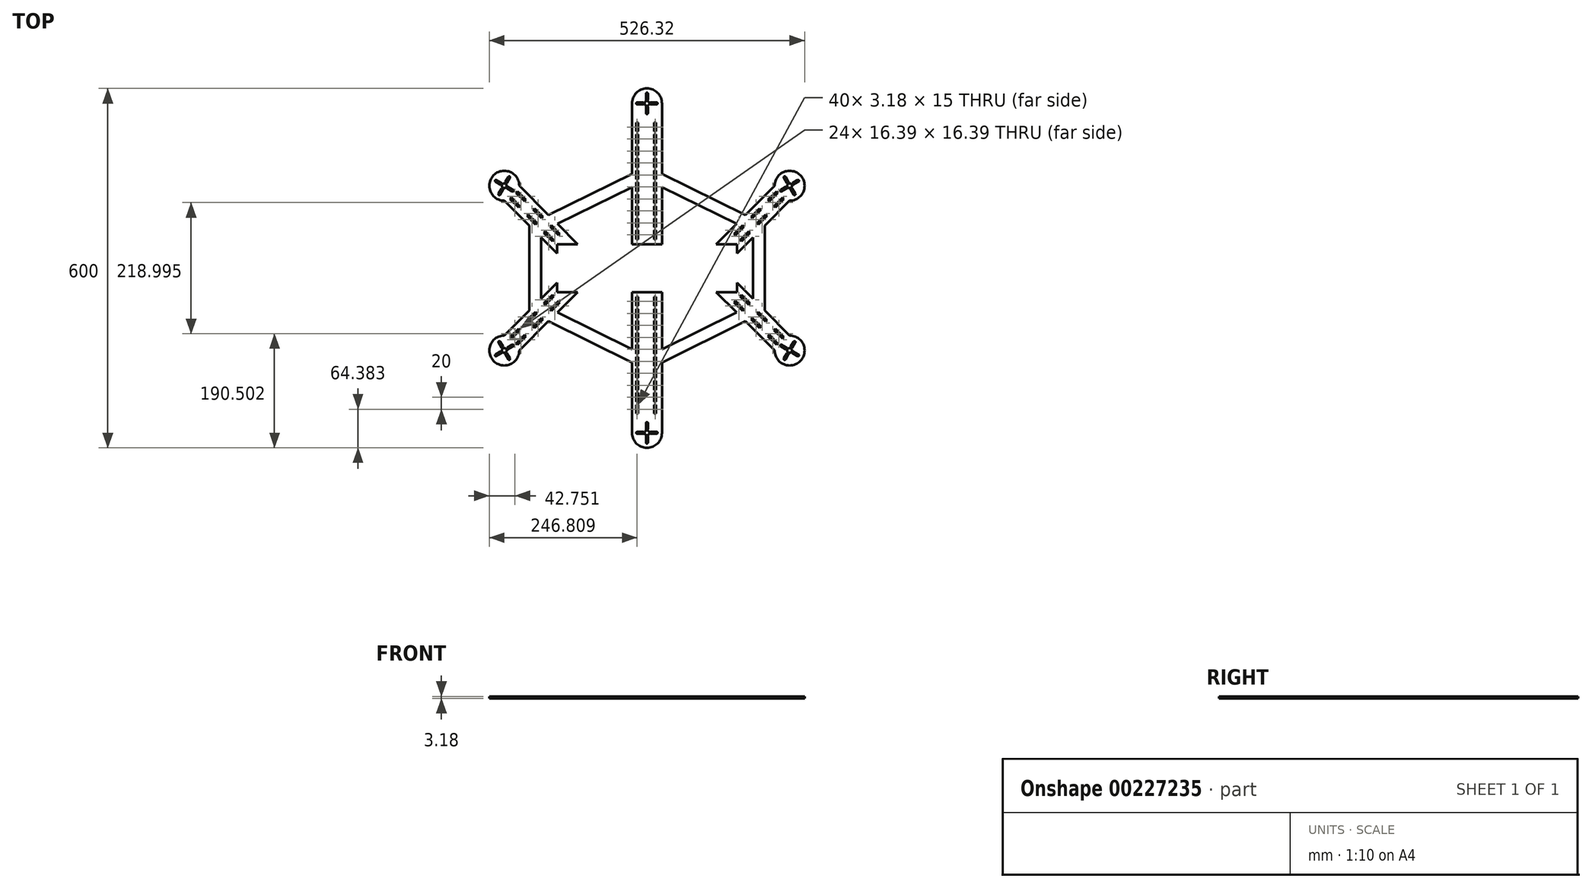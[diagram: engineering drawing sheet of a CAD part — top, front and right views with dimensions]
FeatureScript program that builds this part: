
annotation { "Feature Type Name" : "Feature", "Feature Type Description" : "" }
export const myFeature = defineFeature(function(context is Context, id is Id, definition is map)
    precondition{}
    {
        {
            var Q0;
            Q0=qCreatedBy(makeId("Top.planeOp"),FACE);
            var sketch = newSketch(context, id + "F0", { "sketchPlane" : qUnion([Q0])});
            skPoint(sketch, "E0.middle", {"position": v(0, 0) * mm});
            skCircle(sketch, "E1", {"center": v(0, 275) * mm, "radius": 25 * mm});
            skPoint(sketch, "E1.centerSnap0", {"position": v(0, 301.8) * mm});
            skCircle(sketch, "E2.1.0", {"center": v(-238.16, 137.5) * mm, "radius": 25 * mm});
            skLineSegment(sketch, "E3.bottom", {"start": v(150, -40) * mm, "end": v(-150, -40) * mm});
            skLineSegment(sketch, "E3.top", {"start": v(150, 40) * mm, "end": v(-150, 40) * mm});
            skLineSegment(sketch, "E3.left", {"start": v(150, -40) * mm, "end": v(150, 40) * mm});
            skLineSegment(sketch, "E3.right", {"start": v(-150, -40) * mm, "end": v(-150, 40) * mm});
            skLineSegment(sketch, "E4", {"start": v(-213.16, 137.5) * mm, "end": v(-115.66, 40) * mm});
            skLineSegment(sketch, "E5", {"start": v(-263.16, 137.5) * mm, "end": v(-150, 24.34) * mm});
            skCircle(sketch, "E6.MirrorC", {"center": v(-238.16, -137.5) * mm, "radius": 25 * mm});
            skLineSegment(sketch, "E7", {"start": v(0, 0) * mm, "end": v(0, 86.77) * mm, "construction": true});
            skLineSegment(sketch, "E8.MirrorCS", {"start": v(213.16, 137.5) * mm, "end": v(115.66, 40) * mm});
            skLineSegment(sketch, "E9.MirrorCS", {"start": v(263.16, 137.5) * mm, "end": v(150, 24.34) * mm});
            skCircle(sketch, "E10.MirrorC", {"center": v(238.16, 137.5) * mm, "radius": 25 * mm});
            skCircle(sketch, "E11.MirrorC", {"center": v(238.16, -137.5) * mm, "radius": 25 * mm});
            skLineSegment(sketch, "E12", {"start": v(0, 0) * mm, "end": v(-288.43, 0) * mm, "construction": true});
            skCircle(sketch, "E13.MirrorC", {"center": v(0, -275) * mm, "radius": 25 * mm});
            skLineSegment(sketch, "E14.bottom", {"start": v(-25, 275) * mm, "end": v(25, 275) * mm});
            skLineSegment(sketch, "E14.top", {"start": v(-25, 40) * mm, "end": v(25, 40) * mm});
            skLineSegment(sketch, "E14.left", {"start": v(-25, 275) * mm, "end": v(-25, 40) * mm});
            skLineSegment(sketch, "E14.right", {"start": v(25, 275) * mm, "end": v(25, 40) * mm});
            skLineSegment(sketch, "E15.MirrorCS", {"start": v(-25, -275) * mm, "end": v(-25, -40) * mm});
            skLineSegment(sketch, "E16.MirrorCS", {"start": v(25, -275) * mm, "end": v(25, -40) * mm});
            skLineSegment(sketch, "E17", {"start": v(-25, 157.5) * mm, "end": v(-25, 135.2) * mm});
            skLineSegment(sketch, "E18.MirrorCS", {"start": v(-213.16, -137.5) * mm, "end": v(-115.66, -40) * mm});
            skLineSegment(sketch, "E19.MirrorCS", {"start": v(-263.16, -137.5) * mm, "end": v(-150, -24.34) * mm});
            skLineSegment(sketch, "E20.MirrorCS", {"start": v(263.16, -137.5) * mm, "end": v(150, -24.34) * mm});
            skLineSegment(sketch, "E21.MirrorCS", {"start": v(213.16, -137.5) * mm, "end": v(115.66, -40) * mm});
            skLineSegment(sketch, "E22", {"start": v(-164.4, 88.75) * mm, "end": v(-25, 157.5) * mm});
            skLineSegment(sketch, "E23", {"start": v(-25, 135.2) * mm, "end": v(-149.47, 73.82) * mm});
            skLineSegment(sketch, "E24.MirrorCS", {"start": v(25, 135.2) * mm, "end": v(149.47, 73.82) * mm});
            skLineSegment(sketch, "E25.MirrorCS", {"start": v(164.4, 88.75) * mm, "end": v(25, 157.5) * mm});
            skLineSegment(sketch, "E26.MirrorCS", {"start": v(-25, -135.2) * mm, "end": v(-149.47, -73.82) * mm});
            skLineSegment(sketch, "E27.MirrorCS", {"start": v(-164.4, -88.75) * mm, "end": v(-25, -157.5) * mm});
            skLineSegment(sketch, "E28.MirrorCS", {"start": v(164.4, -88.75) * mm, "end": v(25, -157.5) * mm});
            skLineSegment(sketch, "E29.MirrorCS", {"start": v(25, -135.2) * mm, "end": v(149.47, -73.82) * mm});
            skLineSegment(sketch, "E30", {"start": v(-164.6, -38.94) * mm, "end": v(-188.74, -63.09) * mm});
            skLineSegment(sketch, "E31", {"start": v(-188.74, 63.09) * mm, "end": v(-164.6, 38.94) * mm});
            skLineSegment(sketch, "E32.MirrorCS", {"start": v(188.74, 63.09) * mm, "end": v(164.6, 38.94) * mm});
            skLineSegment(sketch, "E33", {"start": v(-176.67, 51.01) * mm, "end": v(-176.67, -51.01) * mm});
            skLineSegment(sketch, "E34", {"start": v(-196.67, 71.01) * mm, "end": v(-196.67, -71.01) * mm});
            skLineSegment(sketch, "E35.MirrorCS", {"start": v(176.67, 51.01) * mm, "end": v(176.67, -51.01) * mm});
            skLineSegment(sketch, "E36.MirrorCS", {"start": v(196.67, 71.01) * mm, "end": v(196.67, -71.01) * mm});
            skSolve(sketch);
        }
        {
            var Q0;
            Q0 = qSketchRegion(id + "F0", true);
            var Q1;
            {var subQ2=sQuery(id+"F0.wireOp",EDGE,"E14.top");Q1=makeQuery(id+"F0.imprint","IMPRINT",FACE,{"disambiguationData":[TD([[makeQuery(id+"F0.imprint","IMPRINT",EDGE,{"derivedFrom":subQ2}),-1.0]])]});}
            extrude(context, id + "F1", {"entities" : qUnion([Q0, Q1]), "depth" : 3.17 * mm});
        }
        {
            var Q0;
            Q0=makeQuery(id+"F1.opExtrude","CAP_FACE",FACE,{"disambiguationData":[OSD([sQuery(id+"F0.wireOp",EDGE,"E1"),sQuery(id+"F0.wireOp",EDGE,"E2.1.0"),sQuery(id+"F0.wireOp",EDGE,"E3.bottom"),sQuery(id+"F0.wireOp",EDGE,"E3.top"),sQuery(id+"F0.wireOp",EDGE,"E3.left"),sQuery(id+"F0.wireOp",EDGE,"E3.right"),sQuery(id+"F0.wireOp",EDGE,"E4"),sQuery(id+"F0.wireOp",EDGE,"E5"),sQuery(id+"F0.wireOp",EDGE,"E6.MirrorC"),sQuery(id+"F0.wireOp",EDGE,"E8.MirrorCS"),sQuery(id+"F0.wireOp",EDGE,"E9.MirrorCS"),sQuery(id+"F0.wireOp",EDGE,"E10.MirrorC"),sQuery(id+"F0.wireOp",EDGE,"E11.MirrorC"),sQuery(id+"F0.wireOp",EDGE,"E13.MirrorC"),sQuery(id+"F0.wireOp",EDGE,"E14.left"),sQuery(id+"F0.wireOp",EDGE,"E14.right"),sQuery(id+"F0.wireOp",EDGE,"E15.MirrorCS"),sQuery(id+"F0.wireOp",EDGE,"E16.MirrorCS"),sQuery(id+"F0.wireOp",EDGE,"E18.MirrorCS"),sQuery(id+"F0.wireOp",EDGE,"E19.MirrorCS"),sQuery(id+"F0.wireOp",EDGE,"E21.MirrorCS"),sQuery(id+"F0.wireOp",EDGE,"E22"),sQuery(id+"F0.wireOp",EDGE,"E23"),sQuery(id+"F0.wireOp",EDGE,"E24.MirrorCS"),sQuery(id+"F0.wireOp",EDGE,"E25.MirrorCS"),sQuery(id+"F0.wireOp",EDGE,"E26.MirrorCS"),sQuery(id+"F0.wireOp",EDGE,"E27.MirrorCS"),sQuery(id+"F0.wireOp",EDGE,"E28.MirrorCS"),sQuery(id+"F0.wireOp",EDGE,"E29.MirrorCS"),sQuery(id+"F0.wireOp",EDGE,"E30"),sQuery(id+"F0.wireOp",EDGE,"E31"),sQuery(id+"F0.wireOp",EDGE,"E32.MirrorCS"),sQuery(id+"F0.wireOp",EDGE,"E20.MirrorCS"),sQuery(id+"F0.wireOp",EDGE,"E33"),sQuery(id+"F0.wireOp",EDGE,"E34"),sQuery(id+"F0.wireOp",EDGE,"E35.MirrorCS"),sQuery(id+"F0.wireOp",EDGE,"E36.MirrorCS")])],"isStart":false});
            var sketch = newSketch(context, id + "F2", { "sketchPlane" : qUnion([Q0])});
            skLineSegment(sketch, "E37.bottom", {"start": v(-17.94, 243.12) * mm, "end": v(-14.76, 243.12) * mm});
            skLineSegment(sketch, "E37.top", {"start": v(-17.94, 228.12) * mm, "end": v(-14.76, 228.12) * mm});
            skLineSegment(sketch, "E37.left", {"start": v(-17.94, 243.12) * mm, "end": v(-17.94, 228.12) * mm});
            skLineSegment(sketch, "E37.right", {"start": v(-14.76, 243.12) * mm, "end": v(-14.76, 228.12) * mm});
            skLineSegment(sketch, "E38.1.0.0", {"start": v(12.06, 243.12) * mm, "end": v(15.24, 243.12) * mm});
            skLineSegment(sketch, "E38.1.0.1", {"start": v(12.06, 243.12) * mm, "end": v(12.06, 228.12) * mm});
            skLineSegment(sketch, "E38.1.0.2", {"start": v(15.24, 243.12) * mm, "end": v(15.24, 228.12) * mm});
            skLineSegment(sketch, "E38.1.0.3", {"start": v(12.06, 228.12) * mm, "end": v(15.24, 228.12) * mm});
            skLineSegment(sketch, "E38.direction1", {"start": v(-17.94, 243.12) * mm, "end": v(12.06, 243.12) * mm, "construction": true});
            skLineSegment(sketch, "E39.0.1.0", {"start": v(-17.94, 223.12) * mm, "end": v(12.06, 223.12) * mm, "construction": true});
            skLineSegment(sketch, "E39.0.1.1", {"start": v(-14.76, 223.12) * mm, "end": v(-14.76, 208.12) * mm});
            skLineSegment(sketch, "E39.0.1.2", {"start": v(-17.94, 223.12) * mm, "end": v(-17.94, 208.12) * mm});
            skLineSegment(sketch, "E39.0.1.3", {"start": v(15.24, 223.12) * mm, "end": v(15.24, 208.12) * mm});
            skLineSegment(sketch, "E39.0.1.4", {"start": v(12.06, 223.12) * mm, "end": v(12.06, 208.12) * mm});
            skLineSegment(sketch, "E39.0.1.5", {"start": v(12.06, 208.12) * mm, "end": v(15.24, 208.12) * mm});
            skLineSegment(sketch, "E39.0.1.6", {"start": v(-17.94, 223.12) * mm, "end": v(-14.76, 223.12) * mm});
            skLineSegment(sketch, "E39.0.1.7", {"start": v(-17.94, 208.12) * mm, "end": v(-14.76, 208.12) * mm});
            skLineSegment(sketch, "E39.0.1.8", {"start": v(12.06, 223.12) * mm, "end": v(15.24, 223.12) * mm});
            skLineSegment(sketch, "E39.0.2.0", {"start": v(-17.94, 203.12) * mm, "end": v(12.06, 203.12) * mm, "construction": true});
            skLineSegment(sketch, "E39.0.2.1", {"start": v(-14.76, 203.12) * mm, "end": v(-14.76, 188.12) * mm});
            skLineSegment(sketch, "E39.0.2.2", {"start": v(-17.94, 203.12) * mm, "end": v(-17.94, 188.12) * mm});
            skLineSegment(sketch, "E39.0.2.3", {"start": v(15.24, 203.12) * mm, "end": v(15.24, 188.12) * mm});
            skLineSegment(sketch, "E39.0.2.4", {"start": v(12.06, 203.12) * mm, "end": v(12.06, 188.12) * mm});
            skLineSegment(sketch, "E39.0.2.5", {"start": v(12.06, 188.12) * mm, "end": v(15.24, 188.12) * mm});
            skLineSegment(sketch, "E39.0.2.6", {"start": v(-17.94, 203.12) * mm, "end": v(-14.76, 203.12) * mm});
            skLineSegment(sketch, "E39.0.2.7", {"start": v(-17.94, 188.12) * mm, "end": v(-14.76, 188.12) * mm});
            skLineSegment(sketch, "E39.0.2.8", {"start": v(12.06, 203.12) * mm, "end": v(15.24, 203.12) * mm});
            skLineSegment(sketch, "E39.0.3.0", {"start": v(-17.94, 183.12) * mm, "end": v(12.06, 183.12) * mm, "construction": true});
            skLineSegment(sketch, "E39.0.3.1", {"start": v(-14.76, 183.12) * mm, "end": v(-14.76, 168.12) * mm});
            skLineSegment(sketch, "E39.0.3.2", {"start": v(-17.94, 183.12) * mm, "end": v(-17.94, 168.12) * mm});
            skLineSegment(sketch, "E39.0.3.3", {"start": v(15.24, 183.12) * mm, "end": v(15.24, 168.12) * mm});
            skLineSegment(sketch, "E39.0.3.4", {"start": v(12.06, 183.12) * mm, "end": v(12.06, 168.12) * mm});
            skLineSegment(sketch, "E39.0.3.5", {"start": v(12.06, 168.12) * mm, "end": v(15.24, 168.12) * mm});
            skLineSegment(sketch, "E39.0.3.6", {"start": v(-17.94, 183.12) * mm, "end": v(-14.76, 183.12) * mm});
            skLineSegment(sketch, "E39.0.3.7", {"start": v(-17.94, 168.12) * mm, "end": v(-14.76, 168.12) * mm});
            skLineSegment(sketch, "E39.0.3.8", {"start": v(12.06, 183.12) * mm, "end": v(15.24, 183.12) * mm});
            skLineSegment(sketch, "E39.0.4.0", {"start": v(-17.94, 163.12) * mm, "end": v(12.06, 163.12) * mm, "construction": true});
            skLineSegment(sketch, "E39.0.4.1", {"start": v(-14.76, 163.12) * mm, "end": v(-14.76, 148.12) * mm});
            skLineSegment(sketch, "E39.0.4.2", {"start": v(-17.94, 163.12) * mm, "end": v(-17.94, 148.12) * mm});
            skLineSegment(sketch, "E39.0.4.3", {"start": v(15.24, 163.12) * mm, "end": v(15.24, 148.12) * mm});
            skLineSegment(sketch, "E39.0.4.4", {"start": v(12.06, 163.12) * mm, "end": v(12.06, 148.12) * mm});
            skLineSegment(sketch, "E39.0.4.5", {"start": v(12.06, 148.12) * mm, "end": v(15.24, 148.12) * mm});
            skLineSegment(sketch, "E39.0.4.6", {"start": v(-17.94, 163.12) * mm, "end": v(-14.76, 163.12) * mm});
            skLineSegment(sketch, "E39.0.4.7", {"start": v(-17.94, 148.12) * mm, "end": v(-14.76, 148.12) * mm});
            skLineSegment(sketch, "E39.0.4.8", {"start": v(12.06, 163.12) * mm, "end": v(15.24, 163.12) * mm});
            skLineSegment(sketch, "E39.0.5.0", {"start": v(-17.94, 143.12) * mm, "end": v(12.06, 143.12) * mm, "construction": true});
            skLineSegment(sketch, "E39.0.5.1", {"start": v(-14.76, 143.12) * mm, "end": v(-14.76, 128.12) * mm});
            skLineSegment(sketch, "E39.0.5.2", {"start": v(-17.94, 143.12) * mm, "end": v(-17.94, 128.12) * mm});
            skLineSegment(sketch, "E39.0.5.3", {"start": v(15.24, 143.12) * mm, "end": v(15.24, 128.12) * mm});
            skLineSegment(sketch, "E39.0.5.4", {"start": v(12.06, 143.12) * mm, "end": v(12.06, 128.12) * mm});
            skLineSegment(sketch, "E39.0.5.5", {"start": v(12.06, 128.12) * mm, "end": v(15.24, 128.12) * mm});
            skLineSegment(sketch, "E39.0.5.6", {"start": v(-17.94, 143.12) * mm, "end": v(-14.76, 143.12) * mm});
            skLineSegment(sketch, "E39.0.5.7", {"start": v(-17.94, 128.12) * mm, "end": v(-14.76, 128.12) * mm});
            skLineSegment(sketch, "E39.0.5.8", {"start": v(12.06, 143.12) * mm, "end": v(15.24, 143.12) * mm});
            skLineSegment(sketch, "E39.0.6.0", {"start": v(-17.94, 123.12) * mm, "end": v(12.06, 123.12) * mm, "construction": true});
            skLineSegment(sketch, "E39.0.6.1", {"start": v(-14.76, 123.12) * mm, "end": v(-14.76, 108.12) * mm});
            skLineSegment(sketch, "E39.0.6.2", {"start": v(-17.94, 123.12) * mm, "end": v(-17.94, 108.12) * mm});
            skLineSegment(sketch, "E39.0.6.3", {"start": v(15.24, 123.12) * mm, "end": v(15.24, 108.12) * mm});
            skLineSegment(sketch, "E39.0.6.4", {"start": v(12.06, 123.12) * mm, "end": v(12.06, 108.12) * mm});
            skLineSegment(sketch, "E39.0.6.5", {"start": v(12.06, 108.12) * mm, "end": v(15.24, 108.12) * mm});
            skLineSegment(sketch, "E39.0.6.6", {"start": v(-17.94, 123.12) * mm, "end": v(-14.76, 123.12) * mm});
            skLineSegment(sketch, "E39.0.6.7", {"start": v(-17.94, 108.12) * mm, "end": v(-14.76, 108.12) * mm});
            skLineSegment(sketch, "E39.0.6.8", {"start": v(12.06, 123.12) * mm, "end": v(15.24, 123.12) * mm});
            skLineSegment(sketch, "E39.0.7.0", {"start": v(-17.94, 103.12) * mm, "end": v(12.06, 103.12) * mm, "construction": true});
            skLineSegment(sketch, "E39.0.7.1", {"start": v(-14.76, 103.12) * mm, "end": v(-14.76, 88.12) * mm});
            skLineSegment(sketch, "E39.0.7.2", {"start": v(-17.94, 103.12) * mm, "end": v(-17.94, 88.12) * mm});
            skLineSegment(sketch, "E39.0.7.3", {"start": v(15.24, 103.12) * mm, "end": v(15.24, 88.12) * mm});
            skLineSegment(sketch, "E39.0.7.4", {"start": v(12.06, 103.12) * mm, "end": v(12.06, 88.12) * mm});
            skLineSegment(sketch, "E39.0.7.5", {"start": v(12.06, 88.12) * mm, "end": v(15.24, 88.12) * mm});
            skLineSegment(sketch, "E39.0.7.6", {"start": v(-17.94, 103.12) * mm, "end": v(-14.76, 103.12) * mm});
            skLineSegment(sketch, "E39.0.7.7", {"start": v(-17.94, 88.12) * mm, "end": v(-14.76, 88.12) * mm});
            skLineSegment(sketch, "E39.0.7.8", {"start": v(12.06, 103.12) * mm, "end": v(15.24, 103.12) * mm});
            skLineSegment(sketch, "E39.direction1", {"start": v(-17.94, 228.12) * mm, "end": v(7.06, 228.12) * mm, "construction": true});
            skLineSegment(sketch, "E39.direction2", {"start": v(-17.94, 228.12) * mm, "end": v(-17.94, 208.12) * mm, "construction": true});
            skLineSegment(sketch, "E40.MirrorCS", {"start": v(-17.94, -228.12) * mm, "end": v(-14.76, -228.12) * mm});
            skLineSegment(sketch, "E41.MirrorCS", {"start": v(-17.94, -223.12) * mm, "end": v(-14.76, -223.12) * mm});
            skLineSegment(sketch, "E42.MirrorCS", {"start": v(12.06, -223.12) * mm, "end": v(15.24, -223.12) * mm});
            skLineSegment(sketch, "E43.MirrorCS", {"start": v(-17.94, -208.12) * mm, "end": v(-14.76, -208.12) * mm});
            skLineSegment(sketch, "E44.MirrorCS", {"start": v(-17.94, -223.12) * mm, "end": v(-17.94, -208.12) * mm});
            skLineSegment(sketch, "E45.MirrorCS", {"start": v(12.06, -108.12) * mm, "end": v(15.24, -108.12) * mm});
            skLineSegment(sketch, "E46.MirrorCS", {"start": v(-17.94, -108.12) * mm, "end": v(-14.76, -108.12) * mm});
            skLineSegment(sketch, "E47.MirrorCS", {"start": v(12.06, -123.12) * mm, "end": v(15.24, -123.12) * mm});
            skLineSegment(sketch, "E48.MirrorCS", {"start": v(12.06, -228.12) * mm, "end": v(15.24, -228.12) * mm});
            skLineSegment(sketch, "E49.MirrorCS", {"start": v(-17.94, -183.12) * mm, "end": v(-14.76, -183.12) * mm});
            skLineSegment(sketch, "E50.MirrorCS", {"start": v(12.06, -103.12) * mm, "end": v(15.24, -103.12) * mm});
            skLineSegment(sketch, "E51.MirrorCS", {"start": v(-17.94, -148.12) * mm, "end": v(-14.76, -148.12) * mm});
            skLineSegment(sketch, "E52.MirrorCS", {"start": v(-17.94, -143.12) * mm, "end": v(-14.76, -143.12) * mm});
            skLineSegment(sketch, "E53.MirrorCS", {"start": v(-17.94, -103.12) * mm, "end": v(-14.76, -103.12) * mm});
            skLineSegment(sketch, "E54.MirrorCS", {"start": v(12.06, -183.12) * mm, "end": v(15.24, -183.12) * mm});
            skLineSegment(sketch, "E55.MirrorCS", {"start": v(12.06, -203.12) * mm, "end": v(15.24, -203.12) * mm});
            skLineSegment(sketch, "E56.MirrorCS", {"start": v(-17.94, -188.12) * mm, "end": v(-14.76, -188.12) * mm});
            skLineSegment(sketch, "E57.MirrorCS", {"start": v(-17.94, -228.12) * mm, "end": v(-17.94, -208.12) * mm, "construction": true});
            skLineSegment(sketch, "E58.MirrorCS", {"start": v(-14.76, -223.12) * mm, "end": v(-14.76, -208.12) * mm});
            skLineSegment(sketch, "E59.MirrorCS", {"start": v(12.06, -243.12) * mm, "end": v(12.06, -228.12) * mm});
            skLineSegment(sketch, "E60.MirrorCS", {"start": v(12.06, -243.12) * mm, "end": v(15.24, -243.12) * mm});
            skLineSegment(sketch, "E61.MirrorCS", {"start": v(-14.76, -243.12) * mm, "end": v(-14.76, -228.12) * mm});
            skLineSegment(sketch, "E62.MirrorCS", {"start": v(12.06, -223.12) * mm, "end": v(12.06, -208.12) * mm});
            skLineSegment(sketch, "E63.MirrorCS", {"start": v(-17.94, -203.12) * mm, "end": v(-14.76, -203.12) * mm});
            skLineSegment(sketch, "E64.MirrorCS", {"start": v(12.06, -143.12) * mm, "end": v(15.24, -143.12) * mm});
            skLineSegment(sketch, "E65.MirrorCS", {"start": v(-17.94, -123.12) * mm, "end": v(-14.76, -123.12) * mm});
            skLineSegment(sketch, "E66.MirrorCS", {"start": v(-17.94, -128.12) * mm, "end": v(-14.76, -128.12) * mm});
            skLineSegment(sketch, "E67.MirrorCS", {"start": v(12.06, -163.12) * mm, "end": v(15.24, -163.12) * mm});
            skLineSegment(sketch, "E68.MirrorCS", {"start": v(-17.94, -163.12) * mm, "end": v(-14.76, -163.12) * mm});
            skLineSegment(sketch, "E69.MirrorCS", {"start": v(15.24, -223.12) * mm, "end": v(15.24, -208.12) * mm});
            skLineSegment(sketch, "E70.MirrorCS", {"start": v(15.24, -243.12) * mm, "end": v(15.24, -228.12) * mm});
            skLineSegment(sketch, "E71.MirrorCS", {"start": v(-17.94, -243.12) * mm, "end": v(-17.94, -228.12) * mm});
            skLineSegment(sketch, "E72.MirrorCS", {"start": v(-17.94, -243.12) * mm, "end": v(-14.76, -243.12) * mm});
            skLineSegment(sketch, "E73.MirrorCS", {"start": v(12.06, -208.12) * mm, "end": v(15.24, -208.12) * mm});
            skLineSegment(sketch, "E74.MirrorCS", {"start": v(12.06, -188.12) * mm, "end": v(15.24, -188.12) * mm});
            skLineSegment(sketch, "E75.MirrorCS", {"start": v(15.24, -163.12) * mm, "end": v(15.24, -148.12) * mm});
            skLineSegment(sketch, "E76.MirrorCS", {"start": v(-14.76, -123.12) * mm, "end": v(-14.76, -108.12) * mm});
            skLineSegment(sketch, "E77.MirrorCS", {"start": v(12.06, -88.12) * mm, "end": v(15.24, -88.12) * mm});
            skLineSegment(sketch, "E78.MirrorCS", {"start": v(-14.76, -183.12) * mm, "end": v(-14.76, -168.12) * mm});
            skLineSegment(sketch, "E79.MirrorCS", {"start": v(-17.94, -203.12) * mm, "end": v(-17.94, -188.12) * mm});
            skLineSegment(sketch, "E80.MirrorCS", {"start": v(15.24, -203.12) * mm, "end": v(15.24, -188.12) * mm});
            skLineSegment(sketch, "E81.MirrorCS", {"start": v(12.06, -163.12) * mm, "end": v(12.06, -148.12) * mm});
            skLineSegment(sketch, "E82.MirrorCS", {"start": v(-17.94, -123.12) * mm, "end": v(-17.94, -108.12) * mm});
            skLineSegment(sketch, "E83.MirrorCS", {"start": v(15.24, -143.12) * mm, "end": v(15.24, -128.12) * mm});
            skLineSegment(sketch, "E84.MirrorCS", {"start": v(-14.76, -103.12) * mm, "end": v(-14.76, -88.12) * mm});
            skLineSegment(sketch, "E85.MirrorCS", {"start": v(-14.76, -163.12) * mm, "end": v(-14.76, -148.12) * mm});
            skLineSegment(sketch, "E86.MirrorCS", {"start": v(-17.94, -88.12) * mm, "end": v(-14.76, -88.12) * mm});
            skLineSegment(sketch, "E87.MirrorCS", {"start": v(12.06, -183.12) * mm, "end": v(12.06, -168.12) * mm});
            skLineSegment(sketch, "E88.MirrorCS", {"start": v(12.06, -123.12) * mm, "end": v(12.06, -108.12) * mm});
            skLineSegment(sketch, "E89.MirrorCS", {"start": v(-17.94, -168.12) * mm, "end": v(-14.76, -168.12) * mm});
            skLineSegment(sketch, "E90.MirrorCS", {"start": v(15.24, -123.12) * mm, "end": v(15.24, -108.12) * mm});
            skLineSegment(sketch, "E91.MirrorCS", {"start": v(12.06, -143.12) * mm, "end": v(12.06, -128.12) * mm});
            skLineSegment(sketch, "E92.MirrorCS", {"start": v(-17.94, -103.12) * mm, "end": v(-17.94, -88.12) * mm});
            skLineSegment(sketch, "E93.MirrorCS", {"start": v(12.06, -168.12) * mm, "end": v(15.24, -168.12) * mm});
            skLineSegment(sketch, "E94.MirrorCS", {"start": v(-17.94, -143.12) * mm, "end": v(-17.94, -128.12) * mm});
            skLineSegment(sketch, "E95.MirrorCS", {"start": v(12.06, -203.12) * mm, "end": v(12.06, -188.12) * mm});
            skLineSegment(sketch, "E96.MirrorCS", {"start": v(-17.94, -163.12) * mm, "end": v(-17.94, -148.12) * mm});
            skLineSegment(sketch, "E97.MirrorCS", {"start": v(-14.76, -143.12) * mm, "end": v(-14.76, -128.12) * mm});
            skLineSegment(sketch, "E98.MirrorCS", {"start": v(-17.94, -183.12) * mm, "end": v(-17.94, -168.12) * mm});
            skLineSegment(sketch, "E99.MirrorCS", {"start": v(15.24, -183.12) * mm, "end": v(15.24, -168.12) * mm});
            skLineSegment(sketch, "E100.MirrorCS", {"start": v(12.06, -103.12) * mm, "end": v(12.06, -88.12) * mm});
            skLineSegment(sketch, "E101.MirrorCS", {"start": v(-14.76, -203.12) * mm, "end": v(-14.76, -188.12) * mm});
            skLineSegment(sketch, "E102.MirrorCS", {"start": v(12.06, -128.12) * mm, "end": v(15.24, -128.12) * mm});
            skLineSegment(sketch, "E103.MirrorCS", {"start": v(15.24, -103.12) * mm, "end": v(15.24, -88.12) * mm});
            skLineSegment(sketch, "E104.MirrorCS", {"start": v(12.06, -148.12) * mm, "end": v(15.24, -148.12) * mm});
            skLineSegment(sketch, "E105.MirrorCS", {"start": v(-17.94, -223.12) * mm, "end": v(12.06, -223.12) * mm, "construction": true});
            skLineSegment(sketch, "E106.MirrorCS", {"start": v(-17.94, -228.12) * mm, "end": v(7.06, -228.12) * mm, "construction": true});
            skLineSegment(sketch, "E107.MirrorCS", {"start": v(-17.94, -143.12) * mm, "end": v(12.06, -143.12) * mm, "construction": true});
            skLineSegment(sketch, "E108.MirrorCS", {"start": v(-17.94, -243.12) * mm, "end": v(12.06, -243.12) * mm, "construction": true});
            skLineSegment(sketch, "E109.MirrorCS", {"start": v(-17.94, -163.12) * mm, "end": v(12.06, -163.12) * mm, "construction": true});
            skLineSegment(sketch, "E110.MirrorCS", {"start": v(-17.94, -123.12) * mm, "end": v(12.06, -123.12) * mm, "construction": true});
            skLineSegment(sketch, "E111.MirrorCS", {"start": v(-17.94, -103.12) * mm, "end": v(12.06, -103.12) * mm, "construction": true});
            skLineSegment(sketch, "E112.MirrorCS", {"start": v(-17.94, -183.12) * mm, "end": v(12.06, -183.12) * mm, "construction": true});
            skLineSegment(sketch, "E113.MirrorCS", {"start": v(-17.94, -203.12) * mm, "end": v(12.06, -203.12) * mm, "construction": true});
            skLineSegment(sketch, "E114.0.0.8", {"start": v(-17.94, 83.12) * mm, "end": v(12.06, 83.12) * mm, "construction": true});
            skLineSegment(sketch, "E114.3.0.8", {"start": v(-14.76, 83.12) * mm, "end": v(-14.76, 68.12) * mm});
            skLineSegment(sketch, "E114.6.0.8", {"start": v(-17.94, 83.12) * mm, "end": v(-17.94, 68.12) * mm});
            skLineSegment(sketch, "E114.9.0.8", {"start": v(15.24, 83.12) * mm, "end": v(15.24, 68.12) * mm});
            skLineSegment(sketch, "E114.12.0.8", {"start": v(12.06, 83.12) * mm, "end": v(12.06, 68.12) * mm});
            skLineSegment(sketch, "E114.15.0.8", {"start": v(12.06, 68.12) * mm, "end": v(15.24, 68.12) * mm});
            skLineSegment(sketch, "E114.18.0.8", {"start": v(-17.94, 83.12) * mm, "end": v(-14.76, 83.12) * mm});
            skLineSegment(sketch, "E114.21.0.8", {"start": v(-17.94, 68.12) * mm, "end": v(-14.76, 68.12) * mm});
            skLineSegment(sketch, "E114.24.0.8", {"start": v(12.06, 83.12) * mm, "end": v(15.24, 83.12) * mm});
            skLineSegment(sketch, "E114.0.0.9", {"start": v(-17.94, 63.12) * mm, "end": v(12.06, 63.12) * mm, "construction": true});
            skLineSegment(sketch, "E114.3.0.9", {"start": v(-14.76, 63.12) * mm, "end": v(-14.76, 48.12) * mm});
            skLineSegment(sketch, "E114.6.0.9", {"start": v(-17.94, 63.12) * mm, "end": v(-17.94, 48.12) * mm});
            skLineSegment(sketch, "E114.9.0.9", {"start": v(15.24, 63.12) * mm, "end": v(15.24, 48.12) * mm});
            skLineSegment(sketch, "E114.12.0.9", {"start": v(12.06, 63.12) * mm, "end": v(12.06, 48.12) * mm});
            skLineSegment(sketch, "E114.15.0.9", {"start": v(12.06, 48.12) * mm, "end": v(15.24, 48.12) * mm});
            skLineSegment(sketch, "E114.18.0.9", {"start": v(-17.94, 63.12) * mm, "end": v(-14.76, 63.12) * mm});
            skLineSegment(sketch, "E114.21.0.9", {"start": v(-17.94, 48.12) * mm, "end": v(-14.76, 48.12) * mm});
            skLineSegment(sketch, "E114.24.0.9", {"start": v(12.06, 63.12) * mm, "end": v(15.24, 63.12) * mm});
            skLineSegment(sketch, "E115.MirrorCS", {"start": v(12.06, -83.12) * mm, "end": v(15.24, -83.12) * mm});
            skLineSegment(sketch, "E116.MirrorCS", {"start": v(-17.94, -83.12) * mm, "end": v(-14.76, -83.12) * mm});
            skLineSegment(sketch, "E117.MirrorCS", {"start": v(12.06, -63.12) * mm, "end": v(15.24, -63.12) * mm});
            skLineSegment(sketch, "E118.MirrorCS", {"start": v(-17.94, -63.12) * mm, "end": v(-14.76, -63.12) * mm});
            skLineSegment(sketch, "E119.MirrorCS", {"start": v(-17.94, -68.12) * mm, "end": v(-14.76, -68.12) * mm});
            skLineSegment(sketch, "E120.MirrorCS", {"start": v(12.06, -68.12) * mm, "end": v(15.24, -68.12) * mm});
            skLineSegment(sketch, "E121.MirrorCS", {"start": v(-17.94, -48.12) * mm, "end": v(-14.76, -48.12) * mm});
            skLineSegment(sketch, "E122.MirrorCS", {"start": v(12.06, -48.12) * mm, "end": v(15.24, -48.12) * mm});
            skLineSegment(sketch, "E123.MirrorCS", {"start": v(12.06, -83.12) * mm, "end": v(12.06, -68.12) * mm});
            skLineSegment(sketch, "E124.MirrorCS", {"start": v(15.24, -83.12) * mm, "end": v(15.24, -68.12) * mm});
            skLineSegment(sketch, "E125.MirrorCS", {"start": v(-17.94, -83.12) * mm, "end": v(-17.94, -68.12) * mm});
            skLineSegment(sketch, "E126.MirrorCS", {"start": v(-14.76, -83.12) * mm, "end": v(-14.76, -68.12) * mm});
            skLineSegment(sketch, "E127.MirrorCS", {"start": v(-17.94, -63.12) * mm, "end": v(12.06, -63.12) * mm, "construction": true});
            skLineSegment(sketch, "E128.MirrorCS", {"start": v(-17.94, -83.12) * mm, "end": v(12.06, -83.12) * mm, "construction": true});
            skLineSegment(sketch, "E129.MirrorCS", {"start": v(12.06, -63.12) * mm, "end": v(12.06, -48.12) * mm});
            skLineSegment(sketch, "E130.MirrorCS", {"start": v(15.24, -63.12) * mm, "end": v(15.24, -48.12) * mm});
            skLineSegment(sketch, "E131.MirrorCS", {"start": v(-17.94, -63.12) * mm, "end": v(-17.94, -48.12) * mm});
            skLineSegment(sketch, "E132.MirrorCS", {"start": v(-14.76, -63.12) * mm, "end": v(-14.76, -48.12) * mm});
            skSolve(sketch);
        }
        {
            var Q0;
            Q0 = qSketchRegion(id + "F2", true);
            extrude(context, id + "F3", {"entities" : qUnion([Q0]), "operationType" : NewBodyOperationType.REMOVE, "oppositeDirection" : true, "depth" : 25 * mm});
        }
        {
            var Q0;
            Q0=makeQuery(id+"F1.opExtrude","CAP_FACE",FACE,{"disambiguationData":[OSD([sQuery(id+"F0.wireOp",EDGE,"E1"),sQuery(id+"F0.wireOp",EDGE,"E2.1.0"),sQuery(id+"F0.wireOp",EDGE,"E3.bottom"),sQuery(id+"F0.wireOp",EDGE,"E3.top"),sQuery(id+"F0.wireOp",EDGE,"E3.left"),sQuery(id+"F0.wireOp",EDGE,"E3.right"),sQuery(id+"F0.wireOp",EDGE,"E4"),sQuery(id+"F0.wireOp",EDGE,"E5"),sQuery(id+"F0.wireOp",EDGE,"E6.MirrorC"),sQuery(id+"F0.wireOp",EDGE,"E8.MirrorCS"),sQuery(id+"F0.wireOp",EDGE,"E9.MirrorCS"),sQuery(id+"F0.wireOp",EDGE,"E10.MirrorC"),sQuery(id+"F0.wireOp",EDGE,"E11.MirrorC"),sQuery(id+"F0.wireOp",EDGE,"E13.MirrorC"),sQuery(id+"F0.wireOp",EDGE,"E14.left"),sQuery(id+"F0.wireOp",EDGE,"E14.right"),sQuery(id+"F0.wireOp",EDGE,"E15.MirrorCS"),sQuery(id+"F0.wireOp",EDGE,"E16.MirrorCS"),sQuery(id+"F0.wireOp",EDGE,"E18.MirrorCS"),sQuery(id+"F0.wireOp",EDGE,"E19.MirrorCS"),sQuery(id+"F0.wireOp",EDGE,"E21.MirrorCS"),sQuery(id+"F0.wireOp",EDGE,"E22"),sQuery(id+"F0.wireOp",EDGE,"E23"),sQuery(id+"F0.wireOp",EDGE,"E24.MirrorCS"),sQuery(id+"F0.wireOp",EDGE,"E25.MirrorCS"),sQuery(id+"F0.wireOp",EDGE,"E26.MirrorCS"),sQuery(id+"F0.wireOp",EDGE,"E27.MirrorCS"),sQuery(id+"F0.wireOp",EDGE,"E28.MirrorCS"),sQuery(id+"F0.wireOp",EDGE,"E29.MirrorCS"),sQuery(id+"F0.wireOp",EDGE,"E30"),sQuery(id+"F0.wireOp",EDGE,"E31"),sQuery(id+"F0.wireOp",EDGE,"E32.MirrorCS"),sQuery(id+"F0.wireOp",EDGE,"E20.MirrorCS"),sQuery(id+"F0.wireOp",EDGE,"E33"),sQuery(id+"F0.wireOp",EDGE,"E34"),sQuery(id+"F0.wireOp",EDGE,"E35.MirrorCS"),sQuery(id+"F0.wireOp",EDGE,"E36.MirrorCS")])],"isStart":false});
            var sketch = newSketch(context, id + "F4", { "sketchPlane" : qUnion([Q0])});
            skLineSegment(sketch, "E133.bottom", {"start": v(-201.96, 113.8) * mm, "end": v(-204.2, 111.56) * mm});
            skLineSegment(sketch, "E133.top", {"start": v(-216.1, 127.95) * mm, "end": v(-218.35, 125.7) * mm});
            skLineSegment(sketch, "E133.left", {"start": v(-201.96, 113.8) * mm, "end": v(-216.1, 127.95) * mm});
            skLineSegment(sketch, "E133.right", {"start": v(-204.2, 111.56) * mm, "end": v(-218.35, 125.7) * mm});
            skPoint(sketch, "E133.middle", {"position": v(-210.15, 119.75) * mm});
            skLineSegment(sketch, "E134.MirrorCS", {"start": v(-201.96, -113.8) * mm, "end": v(-204.2, -111.56) * mm});
            skLineSegment(sketch, "E135.MirrorCS", {"start": v(-216.1, -127.95) * mm, "end": v(-218.35, -125.7) * mm});
            skLineSegment(sketch, "E136.MirrorCS", {"start": v(-201.96, -113.8) * mm, "end": v(-216.1, -127.95) * mm});
            skLineSegment(sketch, "E137.MirrorCS", {"start": v(-204.2, -111.56) * mm, "end": v(-218.35, -125.7) * mm});
            skPoint(sketch, "E138.MirrorP", {"position": v(-210.15, -119.75) * mm});
            skPoint(sketch, "E139.1.0.0", {"position": v(-181.87, 91.47) * mm});
            skLineSegment(sketch, "E139.1.0.1", {"start": v(-173.68, 85.52) * mm, "end": v(-187.82, 99.66) * mm});
            skLineSegment(sketch, "E139.1.0.2", {"start": v(-175.92, 83.27) * mm, "end": v(-190.06, 97.42) * mm});
            skLineSegment(sketch, "E139.1.0.3", {"start": v(-173.68, 85.52) * mm, "end": v(-175.92, 83.27) * mm});
            skLineSegment(sketch, "E139.1.0.4", {"start": v(-187.82, 99.66) * mm, "end": v(-190.06, 97.42) * mm});
            skPoint(sketch, "E139.2.0.0", {"position": v(-153.59, 63.18) * mm});
            skLineSegment(sketch, "E139.2.0.1", {"start": v(-145.4, 57.24) * mm, "end": v(-159.53, 71.38) * mm});
            skLineSegment(sketch, "E139.2.0.2", {"start": v(-147.64, 55) * mm, "end": v(-161.78, 69.13) * mm});
            skLineSegment(sketch, "E139.2.0.3", {"start": v(-145.4, 57.24) * mm, "end": v(-147.64, 55) * mm});
            skLineSegment(sketch, "E139.2.0.4", {"start": v(-159.53, 71.38) * mm, "end": v(-161.78, 69.13) * mm});
            skLineSegment(sketch, "E139.direction1", {"start": v(-204.2, 111.56) * mm, "end": v(-175.92, 83.27) * mm, "construction": true});
            skLineSegment(sketch, "E140.MirrorCS", {"start": v(-173.68, -85.52) * mm, "end": v(-175.92, -83.27) * mm});
            skLineSegment(sketch, "E141.MirrorCS", {"start": v(-145.4, -57.24) * mm, "end": v(-147.64, -55) * mm});
            skLineSegment(sketch, "E142.MirrorCS", {"start": v(-187.82, -99.66) * mm, "end": v(-190.06, -97.42) * mm});
            skLineSegment(sketch, "E143.MirrorCS", {"start": v(-159.53, -71.38) * mm, "end": v(-161.78, -69.13) * mm});
            skLineSegment(sketch, "E144.MirrorCS", {"start": v(-145.4, -57.24) * mm, "end": v(-159.53, -71.38) * mm});
            skLineSegment(sketch, "E145.MirrorCS", {"start": v(-175.92, -83.27) * mm, "end": v(-190.06, -97.42) * mm});
            skLineSegment(sketch, "E146.MirrorCS", {"start": v(-173.68, -85.52) * mm, "end": v(-187.82, -99.66) * mm});
            skLineSegment(sketch, "E147.MirrorCS", {"start": v(-147.64, -55) * mm, "end": v(-161.78, -69.13) * mm});
            skPoint(sketch, "E148.MirrorP", {"position": v(-153.59, -63.18) * mm});
            skPoint(sketch, "E149.MirrorP", {"position": v(-181.87, -91.47) * mm});
            skLineSegment(sketch, "E150", {"start": v(-225.5, 124.84) * mm, "end": v(-150.52, 49.86) * mm, "construction": true});
            skLineSegment(sketch, "E151.MirrorCS", {"start": v(-214.46, 101.3) * mm, "end": v(-212.22, 103.55) * mm});
            skLineSegment(sketch, "E152.MirrorCS", {"start": v(-186.18, 73.02) * mm, "end": v(-183.93, 75.26) * mm});
            skLineSegment(sketch, "E153.MirrorCS", {"start": v(-228.6, 115.45) * mm, "end": v(-226.36, 117.7) * mm});
            skLineSegment(sketch, "E154.MirrorCS", {"start": v(-172.03, 58.88) * mm, "end": v(-169.79, 61.12) * mm});
            skLineSegment(sketch, "E155.MirrorCS", {"start": v(-157.9, 44.74) * mm, "end": v(-155.65, 46.98) * mm});
            skLineSegment(sketch, "E156.MirrorCS", {"start": v(-200.32, 87.16) * mm, "end": v(-198.07, 89.4) * mm});
            skLineSegment(sketch, "E157.MirrorCS", {"start": v(-183.93, 75.26) * mm, "end": v(-198.07, 89.4) * mm});
            skPoint(sketch, "E158.MirrorP", {"position": v(-220.4, 109.5) * mm});
            skLineSegment(sketch, "E159.MirrorCS", {"start": v(-212.22, 103.55) * mm, "end": v(-226.36, 117.7) * mm});
            skLineSegment(sketch, "E160.MirrorCS", {"start": v(-214.46, 101.3) * mm, "end": v(-228.6, 115.45) * mm});
            skLineSegment(sketch, "E161.MirrorCS", {"start": v(-212.22, 103.55) * mm, "end": v(-183.93, 75.26) * mm, "construction": true});
            skLineSegment(sketch, "E162.MirrorCS", {"start": v(-155.65, 46.98) * mm, "end": v(-169.79, 61.12) * mm});
            skLineSegment(sketch, "E163.MirrorCS", {"start": v(-157.9, 44.74) * mm, "end": v(-172.03, 58.88) * mm});
            skPoint(sketch, "E164.MirrorP", {"position": v(-163.84, 52.93) * mm});
            skPoint(sketch, "E165.MirrorP", {"position": v(-192.12, 81.21) * mm});
            skLineSegment(sketch, "E166.MirrorCS", {"start": v(-186.18, 73.02) * mm, "end": v(-200.32, 87.16) * mm});
            skLineSegment(sketch, "E167.MirrorCS", {"start": v(-186.18, -73.02) * mm, "end": v(-183.93, -75.26) * mm});
            skLineSegment(sketch, "E168.MirrorCS", {"start": v(-214.46, -101.3) * mm, "end": v(-212.22, -103.55) * mm});
            skLineSegment(sketch, "E169.MirrorCS", {"start": v(-228.6, -115.45) * mm, "end": v(-226.36, -117.7) * mm});
            skLineSegment(sketch, "E170.MirrorCS", {"start": v(-200.32, -87.16) * mm, "end": v(-198.07, -89.4) * mm});
            skLineSegment(sketch, "E171.MirrorCS", {"start": v(-172.03, -58.88) * mm, "end": v(-169.79, -61.12) * mm});
            skLineSegment(sketch, "E172.MirrorCS", {"start": v(-157.9, -44.74) * mm, "end": v(-155.65, -46.98) * mm});
            skLineSegment(sketch, "E173.MirrorCS", {"start": v(-183.93, -75.26) * mm, "end": v(-198.07, -89.4) * mm});
            skLineSegment(sketch, "E174.MirrorCS", {"start": v(-212.22, -103.55) * mm, "end": v(-226.36, -117.7) * mm});
            skLineSegment(sketch, "E175.MirrorCS", {"start": v(-155.65, -46.98) * mm, "end": v(-169.79, -61.12) * mm});
            skLineSegment(sketch, "E176.MirrorCS", {"start": v(-157.9, -44.74) * mm, "end": v(-172.03, -58.88) * mm});
            skLineSegment(sketch, "E177.MirrorCS", {"start": v(-186.18, -73.02) * mm, "end": v(-200.32, -87.16) * mm});
            skLineSegment(sketch, "E178.MirrorCS", {"start": v(-214.46, -101.3) * mm, "end": v(-228.6, -115.45) * mm});
            skPoint(sketch, "E179.MirrorP", {"position": v(-220.4, -109.5) * mm});
            skPoint(sketch, "E180.MirrorP", {"position": v(-163.84, -52.93) * mm});
            skPoint(sketch, "E181.MirrorP", {"position": v(-192.12, -81.21) * mm});
            skLineSegment(sketch, "E182.MirrorCS", {"start": v(-212.22, -103.55) * mm, "end": v(-183.93, -75.26) * mm, "construction": true});
            skLineSegment(sketch, "E183.MirrorCS", {"start": v(159.53, -71.38) * mm, "end": v(161.78, -69.13) * mm});
            skLineSegment(sketch, "E184.MirrorCS", {"start": v(173.68, -85.52) * mm, "end": v(175.92, -83.27) * mm});
            skLineSegment(sketch, "E185.MirrorCS", {"start": v(187.82, -99.66) * mm, "end": v(190.06, -97.42) * mm});
            skLineSegment(sketch, "E186.MirrorCS", {"start": v(214.46, 101.3) * mm, "end": v(212.22, 103.55) * mm});
            skLineSegment(sketch, "E187.MirrorCS", {"start": v(173.68, 85.52) * mm, "end": v(175.92, 83.27) * mm});
            skLineSegment(sketch, "E188.MirrorCS", {"start": v(145.4, -57.24) * mm, "end": v(147.64, -55) * mm});
            skLineSegment(sketch, "E189.MirrorCS", {"start": v(173.68, -85.52) * mm, "end": v(187.82, -99.66) * mm});
            skLineSegment(sketch, "E190.MirrorCS", {"start": v(145.4, -57.24) * mm, "end": v(159.53, -71.38) * mm});
            skLineSegment(sketch, "E191.MirrorCS", {"start": v(175.92, -83.27) * mm, "end": v(190.06, -97.42) * mm});
            skLineSegment(sketch, "E192.MirrorCS", {"start": v(147.64, -55) * mm, "end": v(161.78, -69.13) * mm});
            skLineSegment(sketch, "E193.MirrorCS", {"start": v(175.92, 83.27) * mm, "end": v(190.06, 97.42) * mm});
            skLineSegment(sketch, "E194.MirrorCS", {"start": v(216.1, 127.95) * mm, "end": v(218.35, 125.7) * mm});
            skLineSegment(sketch, "E195.MirrorCS", {"start": v(201.96, 113.8) * mm, "end": v(204.2, 111.56) * mm});
            skLineSegment(sketch, "E196.MirrorCS", {"start": v(159.53, 71.38) * mm, "end": v(161.78, 69.13) * mm});
            skLineSegment(sketch, "E197.MirrorCS", {"start": v(145.4, 57.24) * mm, "end": v(147.64, 55) * mm});
            skLineSegment(sketch, "E198.MirrorCS", {"start": v(187.82, 99.66) * mm, "end": v(190.06, 97.42) * mm});
            skLineSegment(sketch, "E199.MirrorCS", {"start": v(200.32, -87.16) * mm, "end": v(198.07, -89.4) * mm});
            skLineSegment(sketch, "E200.MirrorCS", {"start": v(173.68, 85.52) * mm, "end": v(187.82, 99.66) * mm});
            skLineSegment(sketch, "E201.MirrorCS", {"start": v(204.2, 111.56) * mm, "end": v(218.35, 125.7) * mm});
            skLineSegment(sketch, "E202.MirrorCS", {"start": v(201.96, 113.8) * mm, "end": v(216.1, 127.95) * mm});
            skLineSegment(sketch, "E203.MirrorCS", {"start": v(186.18, 73.02) * mm, "end": v(183.93, 75.26) * mm});
            skLineSegment(sketch, "E204.MirrorCS", {"start": v(172.03, -58.88) * mm, "end": v(169.79, -61.12) * mm});
            skLineSegment(sketch, "E205.MirrorCS", {"start": v(145.4, 57.24) * mm, "end": v(159.53, 71.38) * mm});
            skLineSegment(sketch, "E206.MirrorCS", {"start": v(228.6, 115.45) * mm, "end": v(226.36, 117.7) * mm});
            skLineSegment(sketch, "E207.MirrorCS", {"start": v(200.32, 87.16) * mm, "end": v(198.07, 89.4) * mm});
            skLineSegment(sketch, "E208.MirrorCS", {"start": v(172.03, 58.88) * mm, "end": v(169.79, 61.12) * mm});
            skLineSegment(sketch, "E209.MirrorCS", {"start": v(183.93, -75.26) * mm, "end": v(198.07, -89.4) * mm});
            skLineSegment(sketch, "E210.MirrorCS", {"start": v(183.93, 75.26) * mm, "end": v(198.07, 89.4) * mm});
            skLineSegment(sketch, "E211.MirrorCS", {"start": v(214.46, -101.3) * mm, "end": v(212.22, -103.55) * mm});
            skLineSegment(sketch, "E212.MirrorCS", {"start": v(204.2, 111.56) * mm, "end": v(175.92, 83.27) * mm, "construction": true});
            skLineSegment(sketch, "E213.MirrorCS", {"start": v(186.18, -73.02) * mm, "end": v(183.93, -75.26) * mm});
            skLineSegment(sketch, "E214.MirrorCS", {"start": v(204.2, -111.56) * mm, "end": v(218.35, -125.7) * mm});
            skLineSegment(sketch, "E215.MirrorCS", {"start": v(201.96, -113.8) * mm, "end": v(216.1, -127.95) * mm});
            skLineSegment(sketch, "E216.MirrorCS", {"start": v(214.46, -101.3) * mm, "end": v(228.6, -115.45) * mm});
            skLineSegment(sketch, "E217.MirrorCS", {"start": v(216.1, -127.95) * mm, "end": v(218.35, -125.7) * mm});
            skLineSegment(sketch, "E218.MirrorCS", {"start": v(201.96, -113.8) * mm, "end": v(204.2, -111.56) * mm});
            skLineSegment(sketch, "E219.MirrorCS", {"start": v(186.18, 73.02) * mm, "end": v(200.32, 87.16) * mm});
            skLineSegment(sketch, "E220.MirrorCS", {"start": v(155.65, 46.98) * mm, "end": v(169.79, 61.12) * mm});
            skLineSegment(sketch, "E221.MirrorCS", {"start": v(214.46, 101.3) * mm, "end": v(228.6, 115.45) * mm});
            skLineSegment(sketch, "E222.MirrorCS", {"start": v(212.22, 103.55) * mm, "end": v(226.36, 117.7) * mm});
            skLineSegment(sketch, "E223.MirrorCS", {"start": v(155.65, -46.98) * mm, "end": v(169.79, -61.12) * mm});
            skLineSegment(sketch, "E224.MirrorCS", {"start": v(157.9, -44.74) * mm, "end": v(155.65, -46.98) * mm});
            skLineSegment(sketch, "E225.MirrorCS", {"start": v(212.22, -103.55) * mm, "end": v(183.93, -75.26) * mm, "construction": true});
            skLineSegment(sketch, "E226.MirrorCS", {"start": v(212.22, 103.55) * mm, "end": v(183.93, 75.26) * mm, "construction": true});
            skLineSegment(sketch, "E227.MirrorCS", {"start": v(186.18, -73.02) * mm, "end": v(200.32, -87.16) * mm});
            skLineSegment(sketch, "E228.MirrorCS", {"start": v(228.6, -115.45) * mm, "end": v(226.36, -117.7) * mm});
            skLineSegment(sketch, "E229.MirrorCS", {"start": v(157.9, -44.74) * mm, "end": v(172.03, -58.88) * mm});
            skLineSegment(sketch, "E230.MirrorCS", {"start": v(157.9, 44.74) * mm, "end": v(172.03, 58.88) * mm});
            skLineSegment(sketch, "E231.MirrorCS", {"start": v(212.22, -103.55) * mm, "end": v(226.36, -117.7) * mm});
            skLineSegment(sketch, "E232.MirrorCS", {"start": v(157.9, 44.74) * mm, "end": v(155.65, 46.98) * mm});
            skLineSegment(sketch, "E233.MirrorCS", {"start": v(147.64, 55) * mm, "end": v(161.78, 69.13) * mm});
            skPoint(sketch, "E234.MirrorP", {"position": v(210.15, -119.75) * mm});
            skPoint(sketch, "E235.MirrorP", {"position": v(181.87, -91.47) * mm});
            skPoint(sketch, "E236.MirrorP", {"position": v(153.59, -63.18) * mm});
            skPoint(sketch, "E237.MirrorP", {"position": v(181.87, 91.47) * mm});
            skLineSegment(sketch, "E238.MirrorCS", {"start": v(225.5, 124.84) * mm, "end": v(150.52, 49.86) * mm, "construction": true});
            skPoint(sketch, "E239.MirrorP", {"position": v(163.84, 52.93) * mm});
            skPoint(sketch, "E240.MirrorP", {"position": v(220.4, -109.5) * mm});
            skPoint(sketch, "E241.MirrorP", {"position": v(192.12, 81.21) * mm});
            skPoint(sketch, "E242.MirrorP", {"position": v(163.84, -52.93) * mm});
            skPoint(sketch, "E243.MirrorP", {"position": v(153.59, 63.18) * mm});
            skPoint(sketch, "E244.MirrorP", {"position": v(220.4, 109.5) * mm});
            skPoint(sketch, "E245.MirrorP", {"position": v(192.12, -81.21) * mm});
            skPoint(sketch, "E246.MirrorP", {"position": v(210.15, 119.75) * mm});
            skSolve(sketch);
        }
        {
            var Q0;
            Q0 = qSketchRegion(id + "F4", true);
            extrude(context, id + "F5", {"entities" : qUnion([Q0]), "operationType" : NewBodyOperationType.REMOVE, "oppositeDirection" : true, "depth" : 25 * mm});
        }
        {
            var Q0;
            Q0 = qSketchRegion(id + "F2", true);
            extrude(context, id + "F6", {"entities" : qUnion([Q0]), "operationType" : NewBodyOperationType.REMOVE, "oppositeDirection" : true, "depth" : 3.17 * mm});
        }
        {
            var Q0;
            Q0=makeQuery(id+"F1.opExtrude","CAP_FACE",FACE,{"disambiguationData":[OSD([sQuery(id+"F0.wireOp",EDGE,"E1"),sQuery(id+"F0.wireOp",EDGE,"E2.1.0"),sQuery(id+"F0.wireOp",EDGE,"E3.bottom"),sQuery(id+"F0.wireOp",EDGE,"E3.top"),sQuery(id+"F0.wireOp",EDGE,"E3.left"),sQuery(id+"F0.wireOp",EDGE,"E3.right"),sQuery(id+"F0.wireOp",EDGE,"E4"),sQuery(id+"F0.wireOp",EDGE,"E5"),sQuery(id+"F0.wireOp",EDGE,"E6.MirrorC"),sQuery(id+"F0.wireOp",EDGE,"E8.MirrorCS"),sQuery(id+"F0.wireOp",EDGE,"E9.MirrorCS"),sQuery(id+"F0.wireOp",EDGE,"E10.MirrorC"),sQuery(id+"F0.wireOp",EDGE,"E11.MirrorC"),sQuery(id+"F0.wireOp",EDGE,"E13.MirrorC"),sQuery(id+"F0.wireOp",EDGE,"E14.left"),sQuery(id+"F0.wireOp",EDGE,"E14.right"),sQuery(id+"F0.wireOp",EDGE,"E15.MirrorCS"),sQuery(id+"F0.wireOp",EDGE,"E16.MirrorCS"),sQuery(id+"F0.wireOp",EDGE,"E18.MirrorCS"),sQuery(id+"F0.wireOp",EDGE,"E19.MirrorCS"),sQuery(id+"F0.wireOp",EDGE,"E21.MirrorCS"),sQuery(id+"F0.wireOp",EDGE,"E22"),sQuery(id+"F0.wireOp",EDGE,"E23"),sQuery(id+"F0.wireOp",EDGE,"E24.MirrorCS"),sQuery(id+"F0.wireOp",EDGE,"E25.MirrorCS"),sQuery(id+"F0.wireOp",EDGE,"E26.MirrorCS"),sQuery(id+"F0.wireOp",EDGE,"E27.MirrorCS"),sQuery(id+"F0.wireOp",EDGE,"E28.MirrorCS"),sQuery(id+"F0.wireOp",EDGE,"E29.MirrorCS"),sQuery(id+"F0.wireOp",EDGE,"E30"),sQuery(id+"F0.wireOp",EDGE,"E31"),sQuery(id+"F0.wireOp",EDGE,"E32.MirrorCS"),sQuery(id+"F0.wireOp",EDGE,"E20.MirrorCS"),sQuery(id+"F0.wireOp",EDGE,"E33"),sQuery(id+"F0.wireOp",EDGE,"E34"),sQuery(id+"F0.wireOp",EDGE,"E35.MirrorCS"),sQuery(id+"F0.wireOp",EDGE,"E36.MirrorCS")])],"isStart":false});
            var sketch = newSketch(context, id + "F7", { "sketchPlane" : qUnion([Q0])});
            skCircle(sketch, "E247", {"center": v(-22.77, 22.77) * mm, "radius": 1.5 * mm});
            skCircle(sketch, "E248.1.0", {"center": v(22.77, 22.77) * mm, "radius": 1.5 * mm});
            skCircle(sketch, "E248.2.0", {"center": v(22.77, -22.77) * mm, "radius": 1.5 * mm});
            skCircle(sketch, "E248.3.0", {"center": v(-22.77, -22.77) * mm, "radius": 1.5 * mm});
            skPoint(sketch, "E248.center", {"position": v(0, 0) * mm});
            skLineSegment(sketch, "E248.anchor1", {"start": v(0, 0) * mm, "end": v(-22.77, 22.77) * mm, "construction": true});
            skLineSegment(sketch, "E248.anchor2", {"start": v(0, 0) * mm, "end": v(-22.77, -22.77) * mm, "construction": true});
            skSolve(sketch);
        }
        {
            var Q0;
            Q0 = qSketchRegion(id + "F7", true);
            extrude(context, id + "F8", {"entities" : qUnion([Q0]), "operationType" : NewBodyOperationType.REMOVE, "oppositeDirection" : true, "depth" : 25 * mm});
        }
        {
            var Q0;
            Q0=makeQuery(id+"F1.opExtrude","CAP_FACE",FACE,{"disambiguationData":[OSD([sQuery(id+"F0.wireOp",EDGE,"E1"),sQuery(id+"F0.wireOp",EDGE,"E2.1.0"),sQuery(id+"F0.wireOp",EDGE,"E3.bottom"),sQuery(id+"F0.wireOp",EDGE,"E3.top"),sQuery(id+"F0.wireOp",EDGE,"E3.left"),sQuery(id+"F0.wireOp",EDGE,"E3.right"),sQuery(id+"F0.wireOp",EDGE,"E4"),sQuery(id+"F0.wireOp",EDGE,"E5"),sQuery(id+"F0.wireOp",EDGE,"E6.MirrorC"),sQuery(id+"F0.wireOp",EDGE,"E8.MirrorCS"),sQuery(id+"F0.wireOp",EDGE,"E9.MirrorCS"),sQuery(id+"F0.wireOp",EDGE,"E10.MirrorC"),sQuery(id+"F0.wireOp",EDGE,"E11.MirrorC"),sQuery(id+"F0.wireOp",EDGE,"E13.MirrorC"),sQuery(id+"F0.wireOp",EDGE,"E14.left"),sQuery(id+"F0.wireOp",EDGE,"E14.right"),sQuery(id+"F0.wireOp",EDGE,"E15.MirrorCS"),sQuery(id+"F0.wireOp",EDGE,"E16.MirrorCS"),sQuery(id+"F0.wireOp",EDGE,"E18.MirrorCS"),sQuery(id+"F0.wireOp",EDGE,"E19.MirrorCS"),sQuery(id+"F0.wireOp",EDGE,"E21.MirrorCS"),sQuery(id+"F0.wireOp",EDGE,"E22"),sQuery(id+"F0.wireOp",EDGE,"E23"),sQuery(id+"F0.wireOp",EDGE,"E24.MirrorCS"),sQuery(id+"F0.wireOp",EDGE,"E25.MirrorCS"),sQuery(id+"F0.wireOp",EDGE,"E26.MirrorCS"),sQuery(id+"F0.wireOp",EDGE,"E27.MirrorCS"),sQuery(id+"F0.wireOp",EDGE,"E28.MirrorCS"),sQuery(id+"F0.wireOp",EDGE,"E29.MirrorCS"),sQuery(id+"F0.wireOp",EDGE,"E30"),sQuery(id+"F0.wireOp",EDGE,"E31"),sQuery(id+"F0.wireOp",EDGE,"E32.MirrorCS"),sQuery(id+"F0.wireOp",EDGE,"E20.MirrorCS"),sQuery(id+"F0.wireOp",EDGE,"E33"),sQuery(id+"F0.wireOp",EDGE,"E34"),sQuery(id+"F0.wireOp",EDGE,"E35.MirrorCS"),sQuery(id+"F0.wireOp",EDGE,"E36.MirrorCS")])],"isStart":false});
            var sketch = newSketch(context, id + "F9", { "sketchPlane" : qUnion([Q0])});
            skCircle(sketch, "E249", {"center": v(0, 275) * mm, "radius": 4 * mm});
            skLineSegment(sketch, "E250.bottom", {"start": v(1.5, 281.36) * mm, "end": v(-1.5, 281.36) * mm});
            skLineSegment(sketch, "E250.top", {"start": v(1.5, 291.36) * mm, "end": v(-1.5, 291.36) * mm});
            skLineSegment(sketch, "E250.left", {"start": v(1.5, 281.36) * mm, "end": v(1.5, 291.36) * mm});
            skLineSegment(sketch, "E250.right", {"start": v(-1.5, 281.36) * mm, "end": v(-1.5, 291.36) * mm});
            skPoint(sketch, "E250.middle", {"position": v(0, 286.36) * mm});
            skArc(sketch, "E251", {"start": v(-1.5, 281.36) * mm, "mid": v(0, 279.86) * mm, "end": v(1.5, 281.36) * mm});
            skArc(sketch, "E252", {"start": v(1.5, 291.36) * mm, "mid": v(0, 292.86) * mm, "end": v(-1.5, 291.36) * mm});
            skPoint(sketch, "E253.1.0", {"position": v(-11.36, 275) * mm});
            skLineSegment(sketch, "E253.1.1", {"start": v(-6.36, 276.5) * mm, "end": v(-6.36, 273.5) * mm});
            skLineSegment(sketch, "E253.1.2", {"start": v(-16.36, 276.5) * mm, "end": v(-16.36, 273.5) * mm});
            skLineSegment(sketch, "E253.1.3", {"start": v(-6.36, 276.5) * mm, "end": v(-16.36, 276.5) * mm});
            skLineSegment(sketch, "E253.1.4", {"start": v(-6.36, 273.5) * mm, "end": v(-16.36, 273.5) * mm});
            skArc(sketch, "E253.1.5", {"start": v(-6.36, 273.5) * mm, "mid": v(-4.86, 275) * mm, "end": v(-6.36, 276.5) * mm});
            skArc(sketch, "E253.1.6", {"start": v(-16.36, 276.5) * mm, "mid": v(-17.86, 275) * mm, "end": v(-16.36, 273.5) * mm});
            skPoint(sketch, "E253.2.0", {"position": v(0, 263.64) * mm});
            skLineSegment(sketch, "E253.2.1", {"start": v(-1.5, 268.64) * mm, "end": v(1.5, 268.64) * mm});
            skLineSegment(sketch, "E253.2.2", {"start": v(-1.5, 258.64) * mm, "end": v(1.5, 258.64) * mm});
            skLineSegment(sketch, "E253.2.3", {"start": v(-1.5, 268.64) * mm, "end": v(-1.5, 258.64) * mm});
            skLineSegment(sketch, "E253.2.4", {"start": v(1.5, 268.64) * mm, "end": v(1.5, 258.64) * mm});
            skArc(sketch, "E253.2.5", {"start": v(1.5, 268.64) * mm, "mid": v(0, 270.14) * mm, "end": v(-1.5, 268.64) * mm});
            skArc(sketch, "E253.2.6", {"start": v(-1.5, 258.64) * mm, "mid": v(0, 257.14) * mm, "end": v(1.5, 258.64) * mm});
            skPoint(sketch, "E253.3.0", {"position": v(11.36, 275) * mm});
            skLineSegment(sketch, "E253.3.1", {"start": v(6.36, 273.5) * mm, "end": v(6.36, 276.5) * mm});
            skLineSegment(sketch, "E253.3.2", {"start": v(16.36, 273.5) * mm, "end": v(16.36, 276.5) * mm});
            skLineSegment(sketch, "E253.3.3", {"start": v(6.36, 273.5) * mm, "end": v(16.36, 273.5) * mm});
            skLineSegment(sketch, "E253.3.4", {"start": v(6.36, 276.5) * mm, "end": v(16.36, 276.5) * mm});
            skArc(sketch, "E253.3.5", {"start": v(6.36, 276.5) * mm, "mid": v(4.86, 275) * mm, "end": v(6.36, 273.5) * mm});
            skArc(sketch, "E253.3.6", {"start": v(16.36, 273.5) * mm, "mid": v(17.86, 275) * mm, "end": v(16.36, 276.5) * mm});
            skLineSegment(sketch, "E254.1.0", {"start": v(-233.4, 133.02) * mm, "end": v(-224.73, 128.02) * mm});
            skArc(sketch, "E254.1.1", {"start": v(-228.67, 150.9) * mm, "mid": v(-229.22, 152.96) * mm, "end": v(-231.27, 152.4) * mm});
            skArc(sketch, "E254.1.2", {"start": v(-236.27, 143.75) * mm, "mid": v(-235.72, 141.7) * mm, "end": v(-233.67, 142.25) * mm});
            skLineSegment(sketch, "E254.1.3", {"start": v(-236.27, 143.75) * mm, "end": v(-231.27, 152.4) * mm});
            skPoint(sketch, "E254.1.4", {"position": v(-228.31, 131.82) * mm});
            skArc(sketch, "E254.1.5", {"start": v(-247.63, 124.08) * mm, "mid": v(-247.08, 122.03) * mm, "end": v(-245.03, 122.58) * mm});
            skArc(sketch, "E254.1.6", {"start": v(-240.03, 131.24) * mm, "mid": v(-240.58, 133.3) * mm, "end": v(-242.63, 132.74) * mm});
            skLineSegment(sketch, "E254.1.7", {"start": v(-240.03, 131.24) * mm, "end": v(-245.03, 122.58) * mm});
            skLineSegment(sketch, "E254.1.8", {"start": v(-242.63, 132.74) * mm, "end": v(-247.63, 124.08) * mm});
            skLineSegment(sketch, "E254.1.9", {"start": v(-233.67, 142.25) * mm, "end": v(-228.67, 150.9) * mm});
            skArc(sketch, "E254.1.10", {"start": v(-251.56, 146.97) * mm, "mid": v(-253.61, 146.42) * mm, "end": v(-253.06, 144.37) * mm});
            skArc(sketch, "E254.1.11", {"start": v(-244.4, 139.37) * mm, "mid": v(-242.35, 139.92) * mm, "end": v(-242.9, 141.97) * mm});
            skLineSegment(sketch, "E254.1.12", {"start": v(-244.4, 139.37) * mm, "end": v(-253.06, 144.37) * mm});
            skLineSegment(sketch, "E254.1.13", {"start": v(-242.9, 141.97) * mm, "end": v(-251.56, 146.97) * mm});
            skPoint(sketch, "E254.1.14", {"position": v(-243.83, 127.66) * mm});
            skCircle(sketch, "E254.1.15", {"center": v(-238.15, 137.5) * mm, "radius": 4 * mm});
            skPoint(sketch, "E254.1.16", {"position": v(-232.47, 147.33) * mm});
            skPoint(sketch, "E254.1.17", {"position": v(-238.15, 137.5) * mm});
            skLineSegment(sketch, "E254.1.18", {"start": v(-231.9, 135.62) * mm, "end": v(-223.23, 130.62) * mm});
            skArc(sketch, "E254.1.19", {"start": v(-231.9, 135.62) * mm, "mid": v(-233.94, 135.07) * mm, "end": v(-233.4, 133.02) * mm});
            skPoint(sketch, "E254.1.20", {"position": v(-247.98, 143.17) * mm});
            skArc(sketch, "E254.1.21", {"start": v(-224.73, 128.02) * mm, "mid": v(-222.69, 128.57) * mm, "end": v(-223.23, 130.62) * mm});
            skLineSegment(sketch, "E254.1.22", {"start": v(-224.73, 128.02) * mm, "end": v(-223.23, 130.62) * mm});
            skLineSegment(sketch, "E254.1.23", {"start": v(-247.63, 124.08) * mm, "end": v(-245.03, 122.58) * mm});
            skLineSegment(sketch, "E254.1.24", {"start": v(-242.63, 132.74) * mm, "end": v(-240.03, 131.24) * mm});
            skLineSegment(sketch, "E254.1.25", {"start": v(-233.4, 133.02) * mm, "end": v(-231.9, 135.62) * mm});
            skLineSegment(sketch, "E254.1.26", {"start": v(-228.67, 150.9) * mm, "end": v(-231.27, 152.4) * mm});
            skLineSegment(sketch, "E254.1.27", {"start": v(-251.56, 146.97) * mm, "end": v(-253.06, 144.37) * mm});
            skLineSegment(sketch, "E254.1.28", {"start": v(-242.9, 141.97) * mm, "end": v(-244.4, 139.37) * mm});
            skLineSegment(sketch, "E254.1.29", {"start": v(-233.67, 142.25) * mm, "end": v(-236.27, 143.75) * mm});
            skLineSegment(sketch, "E254.2.0", {"start": v(-231.89, -135.62) * mm, "end": v(-223.23, -130.62) * mm});
            skArc(sketch, "E254.2.1", {"start": v(-245.02, -122.59) * mm, "mid": v(-247.07, -122.04) * mm, "end": v(-247.62, -124.09) * mm});
            skArc(sketch, "E254.2.2", {"start": v(-242.62, -132.75) * mm, "mid": v(-240.57, -133.3) * mm, "end": v(-240.02, -131.25) * mm});
            skLineSegment(sketch, "E254.2.3", {"start": v(-242.62, -132.75) * mm, "end": v(-247.62, -124.09) * mm});
            skPoint(sketch, "E254.2.4", {"position": v(-228.3, -131.82) * mm});
            skArc(sketch, "E254.2.5", {"start": v(-231.26, -152.41) * mm, "mid": v(-229.21, -152.96) * mm, "end": v(-228.66, -150.91) * mm});
            skArc(sketch, "E254.2.6", {"start": v(-233.66, -142.25) * mm, "mid": v(-235.71, -141.7) * mm, "end": v(-236.26, -143.75) * mm});
            skLineSegment(sketch, "E254.2.7", {"start": v(-233.66, -142.25) * mm, "end": v(-228.66, -150.91) * mm});
            skLineSegment(sketch, "E254.2.8", {"start": v(-236.26, -143.75) * mm, "end": v(-231.26, -152.41) * mm});
            skLineSegment(sketch, "E254.2.9", {"start": v(-240.02, -131.25) * mm, "end": v(-245.02, -122.59) * mm});
            skArc(sketch, "E254.2.10", {"start": v(-253.06, -144.38) * mm, "mid": v(-253.6, -146.43) * mm, "end": v(-251.56, -146.98) * mm});
            skArc(sketch, "E254.2.11", {"start": v(-242.9, -141.98) * mm, "mid": v(-242.35, -139.93) * mm, "end": v(-244.4, -139.38) * mm});
            skLineSegment(sketch, "E254.2.12", {"start": v(-242.9, -141.98) * mm, "end": v(-251.56, -146.98) * mm});
            skLineSegment(sketch, "E254.2.13", {"start": v(-244.4, -139.38) * mm, "end": v(-253.06, -144.38) * mm});
            skPoint(sketch, "E254.2.14", {"position": v(-232.46, -147.33) * mm});
            skCircle(sketch, "E254.2.15", {"center": v(-238.14, -137.5) * mm, "radius": 4 * mm});
            skPoint(sketch, "E254.2.16", {"position": v(-243.82, -127.67) * mm});
            skPoint(sketch, "E254.2.17", {"position": v(-238.14, -137.5) * mm});
            skLineSegment(sketch, "E254.2.18", {"start": v(-233.39, -133.02) * mm, "end": v(-224.73, -128.02) * mm});
            skArc(sketch, "E254.2.19", {"start": v(-233.39, -133.02) * mm, "mid": v(-233.94, -135.07) * mm, "end": v(-231.89, -135.62) * mm});
            skPoint(sketch, "E254.2.20", {"position": v(-247.98, -143.18) * mm});
            skArc(sketch, "E254.2.21", {"start": v(-223.23, -130.62) * mm, "mid": v(-222.68, -128.57) * mm, "end": v(-224.73, -128.02) * mm});
            skLineSegment(sketch, "E254.2.22", {"start": v(-223.23, -130.62) * mm, "end": v(-224.73, -128.02) * mm});
            skLineSegment(sketch, "E254.2.23", {"start": v(-231.26, -152.41) * mm, "end": v(-228.66, -150.91) * mm});
            skLineSegment(sketch, "E254.2.24", {"start": v(-236.26, -143.75) * mm, "end": v(-233.66, -142.25) * mm});
            skLineSegment(sketch, "E254.2.25", {"start": v(-231.89, -135.62) * mm, "end": v(-233.39, -133.02) * mm});
            skLineSegment(sketch, "E254.2.26", {"start": v(-245.02, -122.59) * mm, "end": v(-247.62, -124.09) * mm});
            skLineSegment(sketch, "E254.2.27", {"start": v(-253.06, -144.38) * mm, "end": v(-251.56, -146.98) * mm});
            skLineSegment(sketch, "E254.2.28", {"start": v(-244.4, -139.38) * mm, "end": v(-242.9, -141.98) * mm});
            skLineSegment(sketch, "E254.2.29", {"start": v(-240.02, -131.25) * mm, "end": v(-242.62, -132.75) * mm});
            skLineSegment(sketch, "E254.3.0", {"start": v(1.52, -268.64) * mm, "end": v(1.52, -258.64) * mm});
            skArc(sketch, "E254.3.1", {"start": v(-16.34, -273.5) * mm, "mid": v(-17.84, -275) * mm, "end": v(-16.34, -276.5) * mm});
            skArc(sketch, "E254.3.2", {"start": v(-6.34, -276.5) * mm, "mid": v(-4.84, -275) * mm, "end": v(-6.34, -273.5) * mm});
            skLineSegment(sketch, "E254.3.3", {"start": v(-6.34, -276.5) * mm, "end": v(-16.34, -276.5) * mm});
            skPoint(sketch, "E254.3.4", {"position": v(0.02, -263.64) * mm});
            skArc(sketch, "E254.3.5", {"start": v(16.37, -276.5) * mm, "mid": v(17.87, -275) * mm, "end": v(16.37, -273.5) * mm});
            skArc(sketch, "E254.3.6", {"start": v(6.37, -273.5) * mm, "mid": v(4.87, -275) * mm, "end": v(6.37, -276.5) * mm});
            skLineSegment(sketch, "E254.3.7", {"start": v(6.37, -273.5) * mm, "end": v(16.37, -273.5) * mm});
            skLineSegment(sketch, "E254.3.8", {"start": v(6.37, -276.5) * mm, "end": v(16.37, -276.5) * mm});
            skLineSegment(sketch, "E254.3.9", {"start": v(-6.34, -273.5) * mm, "end": v(-16.34, -273.5) * mm});
            skArc(sketch, "E254.3.10", {"start": v(-1.48, -291.35) * mm, "mid": v(0.02, -292.85) * mm, "end": v(1.52, -291.35) * mm});
            skArc(sketch, "E254.3.11", {"start": v(1.52, -281.35) * mm, "mid": v(0.02, -279.85) * mm, "end": v(-1.48, -281.35) * mm});
            skLineSegment(sketch, "E254.3.12", {"start": v(1.52, -281.35) * mm, "end": v(1.52, -291.35) * mm});
            skLineSegment(sketch, "E254.3.13", {"start": v(-1.48, -281.35) * mm, "end": v(-1.48, -291.35) * mm});
            skPoint(sketch, "E254.3.14", {"position": v(11.37, -275) * mm});
            skCircle(sketch, "E254.3.15", {"center": v(0.02, -275) * mm, "radius": 4 * mm});
            skPoint(sketch, "E254.3.16", {"position": v(-11.34, -275) * mm});
            skPoint(sketch, "E254.3.17", {"position": v(0.02, -275) * mm});
            skLineSegment(sketch, "E254.3.18", {"start": v(-1.48, -268.64) * mm, "end": v(-1.48, -258.64) * mm});
            skArc(sketch, "E254.3.19", {"start": v(-1.48, -268.64) * mm, "mid": v(0.02, -270.14) * mm, "end": v(1.52, -268.64) * mm});
            skPoint(sketch, "E254.3.20", {"position": v(0.02, -286.35) * mm});
            skArc(sketch, "E254.3.21", {"start": v(1.52, -258.64) * mm, "mid": v(0.02, -257.14) * mm, "end": v(-1.48, -258.64) * mm});
            skLineSegment(sketch, "E254.3.22", {"start": v(1.52, -258.64) * mm, "end": v(-1.48, -258.64) * mm});
            skLineSegment(sketch, "E254.3.23", {"start": v(16.37, -276.5) * mm, "end": v(16.37, -273.5) * mm});
            skLineSegment(sketch, "E254.3.24", {"start": v(6.37, -276.5) * mm, "end": v(6.37, -273.5) * mm});
            skLineSegment(sketch, "E254.3.25", {"start": v(1.52, -268.64) * mm, "end": v(-1.48, -268.64) * mm});
            skLineSegment(sketch, "E254.3.26", {"start": v(-16.34, -273.5) * mm, "end": v(-16.34, -276.5) * mm});
            skLineSegment(sketch, "E254.3.27", {"start": v(-1.48, -291.35) * mm, "end": v(1.52, -291.35) * mm});
            skLineSegment(sketch, "E254.3.28", {"start": v(-1.48, -281.35) * mm, "end": v(1.52, -281.35) * mm});
            skLineSegment(sketch, "E254.3.29", {"start": v(-6.34, -273.5) * mm, "end": v(-6.34, -276.5) * mm});
            skLineSegment(sketch, "E254.4.0", {"start": v(233.41, -133) * mm, "end": v(224.75, -128) * mm});
            skArc(sketch, "E254.4.1", {"start": v(228.69, -150.9) * mm, "mid": v(229.24, -152.95) * mm, "end": v(231.29, -152.4) * mm});
            skArc(sketch, "E254.4.2", {"start": v(236.29, -143.74) * mm, "mid": v(235.74, -141.7) * mm, "end": v(233.69, -142.24) * mm});
            skLineSegment(sketch, "E254.4.3", {"start": v(236.29, -143.74) * mm, "end": v(231.29, -152.4) * mm});
            skPoint(sketch, "E254.4.4", {"position": v(228.33, -131.8) * mm});
            skArc(sketch, "E254.4.5", {"start": v(247.64, -124.07) * mm, "mid": v(247.1, -122.02) * mm, "end": v(245.04, -122.57) * mm});
            skArc(sketch, "E254.4.6", {"start": v(240.04, -131.23) * mm, "mid": v(240.6, -133.28) * mm, "end": v(242.64, -132.73) * mm});
            skLineSegment(sketch, "E254.4.7", {"start": v(240.04, -131.23) * mm, "end": v(245.04, -122.57) * mm});
            skLineSegment(sketch, "E254.4.8", {"start": v(242.64, -132.73) * mm, "end": v(247.64, -124.07) * mm});
            skLineSegment(sketch, "E254.4.9", {"start": v(233.69, -142.24) * mm, "end": v(228.69, -150.9) * mm});
            skArc(sketch, "E254.4.10", {"start": v(251.58, -146.96) * mm, "mid": v(253.63, -146.41) * mm, "end": v(253.08, -144.36) * mm});
            skArc(sketch, "E254.4.11", {"start": v(244.42, -139.36) * mm, "mid": v(242.37, -139.91) * mm, "end": v(242.92, -141.96) * mm});
            skLineSegment(sketch, "E254.4.12", {"start": v(244.42, -139.36) * mm, "end": v(253.08, -144.36) * mm});
            skLineSegment(sketch, "E254.4.13", {"start": v(242.92, -141.96) * mm, "end": v(251.58, -146.96) * mm});
            skPoint(sketch, "E254.4.14", {"position": v(243.84, -127.65) * mm});
            skCircle(sketch, "E254.4.15", {"center": v(238.17, -137.49) * mm, "radius": 4 * mm});
            skPoint(sketch, "E254.4.16", {"position": v(232.49, -147.32) * mm});
            skPoint(sketch, "E254.4.17", {"position": v(238.17, -137.49) * mm});
            skLineSegment(sketch, "E254.4.18", {"start": v(231.91, -135.6) * mm, "end": v(223.25, -130.6) * mm});
            skArc(sketch, "E254.4.19", {"start": v(231.91, -135.6) * mm, "mid": v(233.96, -135.06) * mm, "end": v(233.41, -133) * mm});
            skPoint(sketch, "E254.4.20", {"position": v(248, -143.16) * mm});
            skArc(sketch, "E254.4.21", {"start": v(224.75, -128) * mm, "mid": v(222.7, -128.56) * mm, "end": v(223.25, -130.6) * mm});
            skLineSegment(sketch, "E254.4.22", {"start": v(224.75, -128) * mm, "end": v(223.25, -130.6) * mm});
            skLineSegment(sketch, "E254.4.23", {"start": v(247.64, -124.07) * mm, "end": v(245.04, -122.57) * mm});
            skLineSegment(sketch, "E254.4.24", {"start": v(242.64, -132.73) * mm, "end": v(240.04, -131.23) * mm});
            skLineSegment(sketch, "E254.4.25", {"start": v(233.41, -133) * mm, "end": v(231.91, -135.6) * mm});
            skLineSegment(sketch, "E254.4.26", {"start": v(228.69, -150.9) * mm, "end": v(231.29, -152.4) * mm});
            skLineSegment(sketch, "E254.4.27", {"start": v(251.58, -146.96) * mm, "end": v(253.08, -144.36) * mm});
            skLineSegment(sketch, "E254.4.28", {"start": v(242.92, -141.96) * mm, "end": v(244.42, -139.36) * mm});
            skLineSegment(sketch, "E254.4.29", {"start": v(233.69, -142.24) * mm, "end": v(236.29, -143.74) * mm});
            skLineSegment(sketch, "E254.5.0", {"start": v(231.9, 135.63) * mm, "end": v(223.24, 130.63) * mm});
            skArc(sketch, "E254.5.1", {"start": v(245.04, 122.6) * mm, "mid": v(247.08, 122.05) * mm, "end": v(247.63, 124.1) * mm});
            skArc(sketch, "E254.5.2", {"start": v(242.63, 132.76) * mm, "mid": v(240.58, 133.3) * mm, "end": v(240.04, 131.26) * mm});
            skLineSegment(sketch, "E254.5.3", {"start": v(242.63, 132.76) * mm, "end": v(247.63, 124.1) * mm});
            skPoint(sketch, "E254.5.4", {"position": v(228.32, 131.83) * mm});
            skArc(sketch, "E254.5.5", {"start": v(231.28, 152.42) * mm, "mid": v(229.23, 152.97) * mm, "end": v(228.68, 150.92) * mm});
            skArc(sketch, "E254.5.6", {"start": v(233.68, 142.26) * mm, "mid": v(235.73, 141.71) * mm, "end": v(236.28, 143.76) * mm});
            skLineSegment(sketch, "E254.5.7", {"start": v(233.68, 142.26) * mm, "end": v(228.68, 150.92) * mm});
            skLineSegment(sketch, "E254.5.8", {"start": v(236.28, 143.76) * mm, "end": v(231.28, 152.42) * mm});
            skLineSegment(sketch, "E254.5.9", {"start": v(240.04, 131.26) * mm, "end": v(245.04, 122.6) * mm});
            skArc(sketch, "E254.5.10", {"start": v(253.07, 144.39) * mm, "mid": v(253.62, 146.44) * mm, "end": v(251.57, 146.99) * mm});
            skArc(sketch, "E254.5.11", {"start": v(242.91, 141.99) * mm, "mid": v(242.36, 139.94) * mm, "end": v(244.41, 139.39) * mm});
            skLineSegment(sketch, "E254.5.12", {"start": v(242.91, 141.99) * mm, "end": v(251.57, 146.99) * mm});
            skLineSegment(sketch, "E254.5.13", {"start": v(244.41, 139.39) * mm, "end": v(253.07, 144.39) * mm});
            skPoint(sketch, "E254.5.14", {"position": v(232.48, 147.34) * mm});
            skCircle(sketch, "E254.5.15", {"center": v(238.16, 137.5) * mm, "radius": 4 * mm});
            skPoint(sketch, "E254.5.16", {"position": v(243.83, 127.68) * mm});
            skPoint(sketch, "E254.5.17", {"position": v(238.16, 137.5) * mm});
            skLineSegment(sketch, "E254.5.18", {"start": v(233.4, 133.03) * mm, "end": v(224.74, 128.03) * mm});
            skArc(sketch, "E254.5.19", {"start": v(233.4, 133.03) * mm, "mid": v(233.95, 135.08) * mm, "end": v(231.9, 135.63) * mm});
            skPoint(sketch, "E254.5.20", {"position": v(248, 143.19) * mm});
            skArc(sketch, "E254.5.21", {"start": v(223.24, 130.63) * mm, "mid": v(222.7, 128.58) * mm, "end": v(224.74, 128.03) * mm});
            skLineSegment(sketch, "E254.5.22", {"start": v(223.24, 130.63) * mm, "end": v(224.74, 128.03) * mm});
            skLineSegment(sketch, "E254.5.23", {"start": v(231.28, 152.42) * mm, "end": v(228.68, 150.92) * mm});
            skLineSegment(sketch, "E254.5.24", {"start": v(236.28, 143.76) * mm, "end": v(233.68, 142.26) * mm});
            skLineSegment(sketch, "E254.5.25", {"start": v(231.9, 135.63) * mm, "end": v(233.4, 133.03) * mm});
            skLineSegment(sketch, "E254.5.26", {"start": v(245.04, 122.6) * mm, "end": v(247.63, 124.1) * mm});
            skLineSegment(sketch, "E254.5.27", {"start": v(253.07, 144.39) * mm, "end": v(251.57, 146.99) * mm});
            skLineSegment(sketch, "E254.5.28", {"start": v(244.41, 139.39) * mm, "end": v(242.91, 141.99) * mm});
            skLineSegment(sketch, "E254.5.29", {"start": v(240.04, 131.26) * mm, "end": v(242.63, 132.76) * mm});
            skPoint(sketch, "E254.center", {"position": v(0, 0) * mm});
            skSolve(sketch);
        }
        {
            var Q0;
            Q0 = qSketchRegion(id + "F9", true);
            extrude(context, id + "F10", {"entities" : qUnion([Q0]), "operationType" : NewBodyOperationType.REMOVE, "oppositeDirection" : true, "depth" : 25 * mm});
        }
    });
